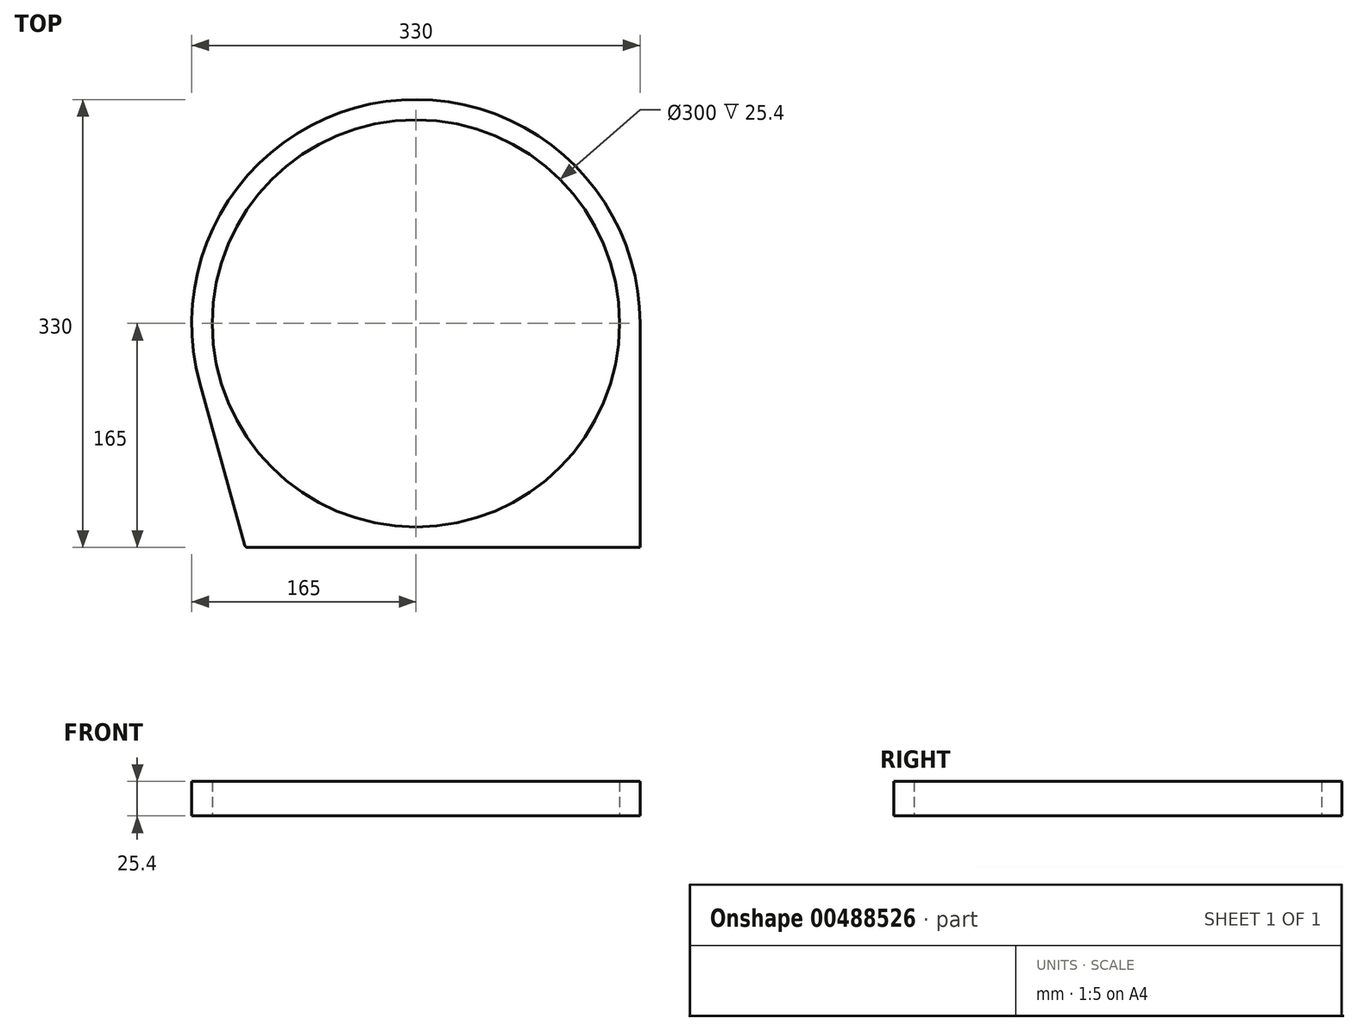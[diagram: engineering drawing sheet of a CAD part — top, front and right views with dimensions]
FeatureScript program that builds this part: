
annotation { "Feature Type Name" : "Feature", "Feature Type Description" : "" }
export const myFeature = defineFeature(function(context is Context, id is Id, definition is map)
    precondition{}
    {
        {
            var Q0;
            Q0=qCreatedBy(makeId("Top.planeOp"),FACE);
            var sketch = newSketch(context, id + "F0", { "sketchPlane" : qUnion([Q0])});
            skLineSegment(sketch, "E0.bottom", {"start": v(165, -165) * mm, "end": v(0, -165) * mm});
            skLineSegment(sketch, "E0.left", {"start": v(165, -165) * mm, "end": v(165, 0) * mm});
            skLineSegment(sketch, "E0.right", {"start": v(-165, -22.4) * mm, "end": v(-165, 0) * mm});
            skPoint(sketch, "E0.middle", {"position": v(0, 0) * mm});
            skCircle(sketch, "E1", {"center": v(0, 0) * mm, "radius": 150 * mm});
            skArc(sketch, "E2", {"start": v(165, 0) * mm, "mid": v(-22.19, 163.5) * mm, "end": v(-159.03, -43.98) * mm});
            skLineSegment(sketch, "E3", {"start": v(0, -165) * mm, "end": v(-124.04, -165) * mm});
            skPoint(sketch, "E4.orphan", {"position": v(165, 165) * mm});
            skPoint(sketch, "E5.orphan", {"position": v(-165, 165) * mm});
            skLineSegment(sketch, "E6", {"start": v(-165, -22.4) * mm, "end": v(-125.97, -163.53) * mm});
            skPoint(sketch, "E7.newPointB", {"position": v(-165, -165) * mm});
            skArc(sketch, "E7.filletArc", {"start": v(-125.97, -163.53) * mm, "mid": v(-125.25, -164.6) * mm, "end": v(-124.04, -165) * mm});
            skSolve(sketch);
        }
        {
            var Q0;
            Q0=makeQuery(id+"F0.imprint","IMPRINT",FACE,{"disambiguationData":[TD([[makeQuery(id+"F0.imprint","IMPRINT",EDGE,{"derivedFrom":sQuery(id+"F0.wireOp",EDGE,"E0.bottom")}),-1.0]])]});
            extrude(context, id + "F1", {"entities" : qUnion([Q0]), "depth" : 25.4 * mm});
        }
    });
